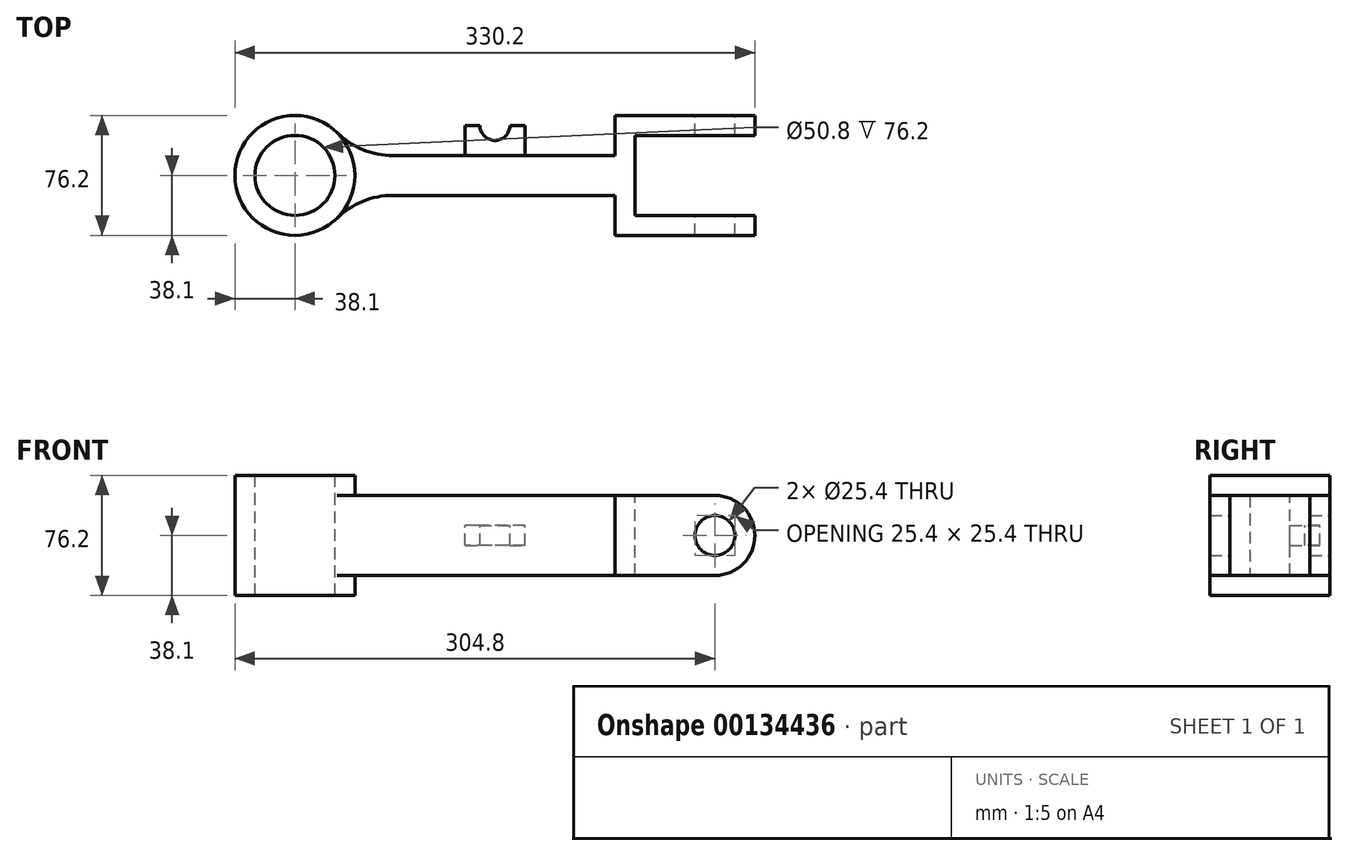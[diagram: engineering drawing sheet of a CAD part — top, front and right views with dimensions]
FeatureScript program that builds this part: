
annotation { "Feature Type Name" : "Feature", "Feature Type Description" : "" }
export const myFeature = defineFeature(function(context is Context, id is Id, definition is map)
    precondition{}
    {
        {
            var Q0;
            Q0=qCreatedBy(makeId("Top.planeOp"),FACE);
            var sketch = newSketch(context, id + "F0", { "sketchPlane" : qUnion([Q0])});
            skCircle(sketch, "E0", {"center": v(0, 0) * mm, "radius": 38.1 * mm});
            skLineSegment(sketch, "E1", {"start": v(35.92, -12.7) * mm, "end": v(203.2, -12.7) * mm});
            skLineSegment(sketch, "E2", {"start": v(35.92, 12.7) * mm, "end": v(203.2, 12.7) * mm});
            skLineSegment(sketch, "E3", {"start": v(203.2, -12.7) * mm, "end": v(203.2, -38.1) * mm});
            skLineSegment(sketch, "E4", {"start": v(203.2, -38.1) * mm, "end": v(279.4, -38.1) * mm});
            skLineSegment(sketch, "E5", {"start": v(279.4, -38.1) * mm, "end": v(279.4, -25.4) * mm});
            skLineSegment(sketch, "E6", {"start": v(279.4, -25.4) * mm, "end": v(215.9, -25.4) * mm});
            skLineSegment(sketch, "E7", {"start": v(215.9, -25.4) * mm, "end": v(215.9, 25.4) * mm});
            skLineSegment(sketch, "E8", {"start": v(215.9, 25.4) * mm, "end": v(279.4, 25.4) * mm});
            skLineSegment(sketch, "E9", {"start": v(279.4, 25.4) * mm, "end": v(279.4, 38.1) * mm});
            skLineSegment(sketch, "E10", {"start": v(279.4, 38.1) * mm, "end": v(203.2, 38.1) * mm});
            skLineSegment(sketch, "E11", {"start": v(203.2, 38.1) * mm, "end": v(203.2, 12.7) * mm});
            skCircle(sketch, "E12", {"center": v(0, 0) * mm, "radius": 25.4 * mm});
            skSolve(sketch);
        }
        {
            var Q0;
            Q0=makeQuery(id+"F0.imprint","IMPRINT",FACE,{"disambiguationData":[TD([[makeQuery(id+"F0.imprint","IMPRINT",EDGE,{"derivedFrom":sQuery(id+"F0.wireOp",EDGE,"E12")}),-1.0]])]});
            var Q1;
            {var subQ0=sQuery(id+"F0.wireOp",EDGE,"E1");Q1=makeQuery(id+"F0.imprint","IMPRINT",FACE,{"disambiguationData":[TD([[makeQuery(id+"F0.imprint","IMPRINT",EDGE,{"derivedFrom":subQ0}),1.0]])]});}
            extrude(context, id + "F1", {"entities" : qUnion([Q0, Q1]), "oppositeDirection" : true, "depth" : 76.2 * mm});
        }
        {
            var Q0;
            Q0=makeQuery(id+"F1.opExtrude","CAP_FACE",FACE,{"disambiguationData":[OSD([sQuery(id+"F0.wireOp",EDGE,"E0"),sQuery(id+"F0.wireOp",EDGE,"E1"),sQuery(id+"F0.wireOp",EDGE,"E2"),sQuery(id+"F0.wireOp",EDGE,"E3"),sQuery(id+"F0.wireOp",EDGE,"E4"),sQuery(id+"F0.wireOp",EDGE,"E5"),sQuery(id+"F0.wireOp",EDGE,"E6"),sQuery(id+"F0.wireOp",EDGE,"E7"),sQuery(id+"F0.wireOp",EDGE,"E8"),sQuery(id+"F0.wireOp",EDGE,"E9"),sQuery(id+"F0.wireOp",EDGE,"E10"),sQuery(id+"F0.wireOp",EDGE,"E11"),sQuery(id+"F0.wireOp",EDGE,"E12")])],"isStart":true});
            var sketch = newSketch(context, id + "F2", { "sketchPlane" : qUnion([Q0])});
            skLineSegment(sketch, "E13", {"start": v(279.4, 25.4) * mm, "end": v(279.4, 38.1) * mm});
            skLineSegment(sketch, "E14", {"start": v(279.4, 38.1) * mm, "end": v(203.2, 38.1) * mm});
            skLineSegment(sketch, "E15", {"start": v(203.2, 38.1) * mm, "end": v(203.2, 12.7) * mm});
            skLineSegment(sketch, "E16", {"start": v(203.2, 12.7) * mm, "end": v(35.92, 12.7) * mm});
            skLineSegment(sketch, "E17", {"start": v(279.4, 25.4) * mm, "end": v(215.9, 25.4) * mm});
            skLineSegment(sketch, "E18", {"start": v(215.9, 25.4) * mm, "end": v(215.9, -25.4) * mm});
            skLineSegment(sketch, "E19", {"start": v(215.9, -25.4) * mm, "end": v(279.4, -25.4) * mm});
            skLineSegment(sketch, "E20", {"start": v(279.4, -25.4) * mm, "end": v(279.4, -38.1) * mm});
            skLineSegment(sketch, "E21", {"start": v(279.4, -38.1) * mm, "end": v(203.2, -38.1) * mm});
            skLineSegment(sketch, "E22", {"start": v(203.2, -38.1) * mm, "end": v(203.2, -12.7) * mm});
            skLineSegment(sketch, "E23", {"start": v(203.2, -12.7) * mm, "end": v(35.92, -12.7) * mm});
            skLineSegment(sketch, "E24", {"start": v(35.92, 12.7) * mm, "end": v(35.92, -12.7) * mm});
            skSolve(sketch);
        }
        {
            var Q0;
            Q0 = qSketchRegion(id + "F2", true);
            extrude(context, id + "F3", {"entities" : qUnion([Q0]), "operationType" : NewBodyOperationType.REMOVE, "oppositeDirection" : true, "depth" : 12.7 * mm});
        }
        {
            var Q0;
            Q0=makeQuery(id+"F1.opExtrude","CAP_FACE",FACE,{"disambiguationData":[OSD([sQuery(id+"F0.wireOp",EDGE,"E0"),sQuery(id+"F0.wireOp",EDGE,"E1"),sQuery(id+"F0.wireOp",EDGE,"E2"),sQuery(id+"F0.wireOp",EDGE,"E3"),sQuery(id+"F0.wireOp",EDGE,"E4"),sQuery(id+"F0.wireOp",EDGE,"E5"),sQuery(id+"F0.wireOp",EDGE,"E6"),sQuery(id+"F0.wireOp",EDGE,"E7"),sQuery(id+"F0.wireOp",EDGE,"E8"),sQuery(id+"F0.wireOp",EDGE,"E9"),sQuery(id+"F0.wireOp",EDGE,"E10"),sQuery(id+"F0.wireOp",EDGE,"E11"),sQuery(id+"F0.wireOp",EDGE,"E12")])],"isStart":false});
            var sketch = newSketch(context, id + "F4", { "sketchPlane" : qUnion([Q0])});
            skLineSegment(sketch, "E25", {"start": v(279.4, 38.1) * mm, "end": v(203.2, 38.1) * mm});
            skLineSegment(sketch, "E26", {"start": v(203.2, 38.1) * mm, "end": v(203.2, 12.7) * mm});
            skLineSegment(sketch, "E27", {"start": v(203.2, 12.7) * mm, "end": v(35.92, 12.7) * mm});
            skLineSegment(sketch, "E28", {"start": v(35.92, 12.7) * mm, "end": v(35.92, -12.7) * mm});
            skLineSegment(sketch, "E29", {"start": v(35.92, -12.7) * mm, "end": v(203.2, -12.7) * mm});
            skLineSegment(sketch, "E30", {"start": v(203.2, -12.7) * mm, "end": v(203.2, -38.1) * mm});
            skLineSegment(sketch, "E31", {"start": v(203.2, -38.1) * mm, "end": v(279.4, -38.1) * mm});
            skLineSegment(sketch, "E32", {"start": v(279.4, -38.1) * mm, "end": v(279.4, -25.4) * mm});
            skLineSegment(sketch, "E33", {"start": v(279.4, -25.4) * mm, "end": v(215.9, -25.4) * mm});
            skLineSegment(sketch, "E34", {"start": v(215.9, -25.4) * mm, "end": v(215.9, 25.4) * mm});
            skLineSegment(sketch, "E35", {"start": v(215.9, 25.4) * mm, "end": v(279.4, 25.4) * mm});
            skLineSegment(sketch, "E36", {"start": v(279.4, 25.4) * mm, "end": v(279.4, 38.1) * mm});
            skSolve(sketch);
        }
        {
            var Q0;
            Q0 = qSketchRegion(id + "F4", true);
            extrude(context, id + "F5", {"entities" : qUnion([Q0]), "operationType" : NewBodyOperationType.REMOVE, "oppositeDirection" : true, "depth" : 12.7 * mm});
        }
        {
            var Q0;
            Q0=makeQuery(id+"F5.boolean.opBoolean","SPLIT",EDGE,{"derivedFrom":makeQuery(id+"F3.boolean.opBoolean","SPLIT",EDGE,{"derivedFrom":makeQuery(id+"F1.opExtrude","SWEPT_EDGE",EDGE,{"disambiguationData":[OSD([sQuery(id+"F0.wireOp",EDGE,"E0"),sQuery(id+"F0.wireOp",EDGE,"E1")])]})})});
            var Q1;
            Q1=makeQuery(id+"F5.boolean.opBoolean","SPLIT",EDGE,{"derivedFrom":makeQuery(id+"F3.boolean.opBoolean","SPLIT",EDGE,{"derivedFrom":makeQuery(id+"F1.opExtrude","SWEPT_EDGE",EDGE,{"disambiguationData":[OSD([sQuery(id+"F0.wireOp",EDGE,"E0"),sQuery(id+"F0.wireOp",EDGE,"E2")])]})})});
            fillet(context, id + "F6", {"entities" : qUnion([Q0, Q1]), "radius" : 50.8 * mm, "tangentPropagation" : true, "allowEdgeOverflow" : false});
        }
        {
            var Q0;
            Q0=makeQuery(id+"F1.opExtrude","CAP_FACE",FACE,{"disambiguationData":[OSD([sQuery(id+"F0.wireOp",EDGE,"E0"),sQuery(id+"F0.wireOp",EDGE,"E1"),sQuery(id+"F0.wireOp",EDGE,"E2"),sQuery(id+"F0.wireOp",EDGE,"E3"),sQuery(id+"F0.wireOp",EDGE,"E4"),sQuery(id+"F0.wireOp",EDGE,"E5"),sQuery(id+"F0.wireOp",EDGE,"E6"),sQuery(id+"F0.wireOp",EDGE,"E7"),sQuery(id+"F0.wireOp",EDGE,"E8"),sQuery(id+"F0.wireOp",EDGE,"E9"),sQuery(id+"F0.wireOp",EDGE,"E10"),sQuery(id+"F0.wireOp",EDGE,"E11"),sQuery(id+"F0.wireOp",EDGE,"E12")])],"isStart":true});
            var sketch = newSketch(context, id + "F7", { "sketchPlane" : qUnion([Q0])});
            skCircle(sketch, "E37", {"center": v(0, 0) * mm, "radius": 38.1 * mm});
            skLineSegment(sketch, "E38", {"start": v(35.92, -12.7) * mm, "end": v(35.92, 12.7) * mm});
            skSolve(sketch);
        }
        {
            var Q0;
            {var subQ0=sQuery(id+"F7.wireOp",EDGE,"E38");Q0=makeQuery(id+"F7.imprint","IMPRINT",FACE,{"disambiguationData":[TD([[makeQuery(id+"F7.imprint","IMPRINT",EDGE,{"derivedFrom":subQ0}),1.0]])]});}
            extrude(context, id + "F8", {"entities" : qUnion([Q0]), "operationType" : NewBodyOperationType.ADD, "oppositeDirection" : true, "depth" : 76.2 * mm});
        }
        {
            var Q0;
            Q0=makeQuery(id+"F1.opExtrude","SWEPT_FACE",FACE,{"disambiguationData":[OSD([sQuery(id+"F0.wireOp",EDGE,"E4")])]});
            var sketch = newSketch(context, id + "F9", { "sketchPlane" : qUnion([Q0])});
            skLineSegment(sketch, "E39", {"start": v(266.7, -12.7) * mm, "end": v(203.2, -12.7) * mm});
            skLineSegment(sketch, "E40", {"start": v(203.2, -12.7) * mm, "end": v(203.2, -63.5) * mm});
            skLineSegment(sketch, "E41", {"start": v(203.2, -63.5) * mm, "end": v(266.7, -63.5) * mm});
            skArc(sketch, "E42", {"start": v(266.7, -12.7) * mm, "mid": v(292.1, -38.1) * mm, "end": v(266.7, -63.5) * mm});
            skSolve(sketch);
        }
        {
            var Q0;
            Q0 = qSketchRegion(id + "F9", true);
            extrude(context, id + "F10", {"entities" : qUnion([Q0]), "operationType" : NewBodyOperationType.ADD, "oppositeDirection" : true, "depth" : 12.7 * mm});
        }
        {
            var Q0;
            Q0=makeQuery(id+"F10.boolean.opBoolean","MERGE",FACE,{"derivedFrom":[makeQuery(id+"F1.opExtrude","SWEPT_FACE",FACE,{"disambiguationData":[OSD([sQuery(id+"F0.wireOp",EDGE,"E4")])]}),makeQuery(id+"F10.opExtrude","CAP_FACE",FACE,{"disambiguationData":[OSD([sQuery(id+"F9.wireOp",EDGE,"E39"),sQuery(id+"F9.wireOp",EDGE,"E40"),sQuery(id+"F9.wireOp",EDGE,"E41"),sQuery(id+"F9.wireOp",EDGE,"E42")])],"isStart":true})]});
            var sketch = newSketch(context, id + "F11", { "sketchPlane" : qUnion([Q0])});
            skLineSegment(sketch, "E43", {"start": v(279.4, -60.1) * mm, "end": v(279.4, -63.5) * mm});
            skLineSegment(sketch, "E44", {"start": v(279.4, -63.5) * mm, "end": v(266.71, -63.5) * mm});
            skArc(sketch, "E45.0", {"start": v(266.7, -12.7) * mm, "mid": v(292.1, -38.1) * mm, "end": v(266.7, -63.5) * mm});
            skLineSegment(sketch, "E46", {"start": v(266.7, -12.7) * mm, "end": v(279.4, -12.7) * mm});
            skLineSegment(sketch, "E47", {"start": v(279.4, -12.7) * mm, "end": v(279.4, -16.1) * mm});
            skSolve(sketch);
        }
        {
            var Q0;
            Q0 = qSketchRegion(id + "F11", true);
            var Q1;
            {var subQ0=sQuery(id+"F9.wireOp",EDGE,"E42");var subQ1=makeQuery(id+"F3.boolean.opBoolean","COPY",EDGE,{"derivedFrom":makeQuery(id+"F3.opExtrude","CAP_EDGE",EDGE,{"disambiguationData":[OSD([sQuery(id+"F2.wireOp",EDGE,"E21")])],"isStart":false})});var subQ2=makeQuery(id+"F9.imprint","INTERSECT",VERTEX,{"derivedFrom":[subQ1,sQuery(id+"F9.wireOp",EDGE,"E39"),subQ0]});Q1=makeQuery(id+"F9.imprint","IMPRINT",FACE,{"disambiguationData":[TD([[makeQuery(id+"F9.imprint","IMPRINT",EDGE,{"disambiguationData":[TD([[subQ2,-1.0]])],"derivedFrom":subQ0}),1.0]])]});}
            var Q2;
            {var subQ0=sQuery(id+"F9.wireOp",EDGE,"E42");var subQ1=makeQuery(id+"F5.boolean.opBoolean","COPY",EDGE,{"derivedFrom":makeQuery(id+"F5.opExtrude","CAP_EDGE",EDGE,{"disambiguationData":[OSD([sQuery(id+"F4.wireOp",EDGE,"E25")])],"isStart":false})});var subQ2=makeQuery(id+"F9.imprint","INTERSECT",VERTEX,{"derivedFrom":[subQ1,sQuery(id+"F9.wireOp",EDGE,"E41"),subQ0]});Q2=makeQuery(id+"F9.imprint","IMPRINT",FACE,{"disambiguationData":[TD([[makeQuery(id+"F9.imprint","IMPRINT",EDGE,{"disambiguationData":[TD([[subQ2,1.0]])],"derivedFrom":subQ0}),1.0]])]});}
            extrude(context, id + "F12", {"entities" : qUnion([Q0, Q1, Q2]), "operationType" : NewBodyOperationType.REMOVE, "oppositeDirection" : true, "depth" : 84.6 * mm});
        }
        {
            var Q0;
            Q0=makeQuery(id+"F1.opExtrude","SWEPT_FACE",FACE,{"disambiguationData":[OSD([sQuery(id+"F0.wireOp",EDGE,"E10")])]});
            var sketch = newSketch(context, id + "F13", { "sketchPlane" : qUnion([Q0])});
            skArc(sketch, "E48.0", {"start": v(-266.7, -12.7) * mm, "mid": v(-292.1, -38.1) * mm, "end": v(-266.7, -63.5) * mm});
            skLineSegment(sketch, "E49", {"start": v(-279.4, -16.1) * mm, "end": v(-279.4, -60.1) * mm});
            skSolve(sketch);
        }
        {
            var Q0;
            Q0 = qSketchRegion(id + "F13", true);
            extrude(context, id + "F14", {"entities" : qUnion([Q0]), "operationType" : NewBodyOperationType.ADD, "oppositeDirection" : true, "depth" : 12.7 * mm});
        }
        {
            var Q0;
            Q0=makeQuery(id+"F14.boolean.opBoolean","MERGE",FACE,{"derivedFrom":[makeQuery(id+"F1.opExtrude","SWEPT_FACE",FACE,{"disambiguationData":[OSD([sQuery(id+"F0.wireOp",EDGE,"E10")])]}),makeQuery(id+"F14.opExtrude","CAP_FACE",FACE,{"disambiguationData":[OSD([sQuery(id+"F13.wireOp",EDGE,"E48.0"),sQuery(id+"F13.wireOp",EDGE,"E49")])],"isStart":true})]});
            var sketch = newSketch(context, id + "F15", { "sketchPlane" : qUnion([Q0])});
            skCircle(sketch, "E50", {"center": v(-266.7, -38.1) * mm, "radius": 12.7 * mm});
            skSolve(sketch);
        }
        {
            var Q0;
            Q0 = qSketchRegion(id + "F15", true);
            extrude(context, id + "F16", {"entities" : qUnion([Q0]), "operationType" : NewBodyOperationType.REMOVE, "endBound" : BoundingType.THROUGH_ALL, "oppositeDirection" : true, "depth" : 25.4 * mm});
        }
        {
            var Q0;
            Q0=makeQuery(id+"F3.boolean.opBoolean","COPY",FACE,{"derivedFrom":makeQuery(id+"F3.opExtrude","CAP_FACE",FACE,{"disambiguationData":[OSD([sQuery(id+"F2.wireOp",EDGE,"E13"),sQuery(id+"F2.wireOp",EDGE,"E14"),sQuery(id+"F2.wireOp",EDGE,"E15"),sQuery(id+"F2.wireOp",EDGE,"E16"),sQuery(id+"F2.wireOp",EDGE,"E17"),sQuery(id+"F2.wireOp",EDGE,"E18"),sQuery(id+"F2.wireOp",EDGE,"E19"),sQuery(id+"F2.wireOp",EDGE,"E20"),sQuery(id+"F2.wireOp",EDGE,"E21"),sQuery(id+"F2.wireOp",EDGE,"E22"),sQuery(id+"F2.wireOp",EDGE,"E23"),sQuery(id+"F2.wireOp",EDGE,"E24")])],"isStart":false})});
            var sketch = newSketch(context, id + "F17", { "sketchPlane" : qUnion([Q0])});
            skLineSegment(sketch, "E51", {"start": v(107.95, 12.7) * mm, "end": v(107.95, 31.75) * mm});
            skLineSegment(sketch, "E52", {"start": v(107.95, 31.75) * mm, "end": v(146.05, 31.75) * mm});
            skLineSegment(sketch, "E53", {"start": v(146.05, 31.75) * mm, "end": v(146.05, 12.7) * mm});
            skLineSegment(sketch, "E54", {"start": v(146.05, 12.7) * mm, "end": v(107.95, 12.7) * mm});
            skArc(sketch, "E55", {"start": v(107.95, 31.75) * mm, "mid": v(127, 50.8) * mm, "end": v(146.05, 31.75) * mm});
            skCircle(sketch, "E56", {"center": v(127, 31.75) * mm, "radius": 9.53 * mm});
            skSolve(sketch);
        }
        {
            var Q0;
            {var subQ5=sQuery(id+"F17.wireOp",EDGE,"E51");Q0=makeQuery(id+"F17.imprint","IMPRINT",FACE,{"disambiguationData":[TD([[makeQuery(id+"F17.imprint","IMPRINT",EDGE,{"derivedFrom":subQ5}),-1.0]])]});}
            var Q1;
            {var subQ0=sQuery(id+"F17.wireOp",EDGE,"E55");Q1=makeQuery(id+"F17.imprint","IMPRINT",FACE,{"disambiguationData":[TD([[makeQuery(id+"F17.imprint","IMPRINT",EDGE,{"derivedFrom":subQ0}),-1.0]])]});}
            extrude(context, id + "F18", {"entities" : qUnion([Q0, Q1]), "operationType" : NewBodyOperationType.ADD, "oppositeDirection" : true, "depth" : 50.8 * mm});
        }
        {
            var Q0;
            Q0=makeQuery(id+"F18.boolean.opBoolean","MERGE",FACE,{"derivedFrom":[makeQuery(id+"F5.boolean.opBoolean","COPY",FACE,{"derivedFrom":makeQuery(id+"F5.opExtrude","CAP_FACE",FACE,{"disambiguationData":[OSD([sQuery(id+"F4.wireOp",EDGE,"E25"),sQuery(id+"F4.wireOp",EDGE,"E26"),sQuery(id+"F4.wireOp",EDGE,"E27"),sQuery(id+"F4.wireOp",EDGE,"E28"),sQuery(id+"F4.wireOp",EDGE,"E29"),sQuery(id+"F4.wireOp",EDGE,"E30"),sQuery(id+"F4.wireOp",EDGE,"E31"),sQuery(id+"F4.wireOp",EDGE,"E32"),sQuery(id+"F4.wireOp",EDGE,"E33"),sQuery(id+"F4.wireOp",EDGE,"E34"),sQuery(id+"F4.wireOp",EDGE,"E35"),sQuery(id+"F4.wireOp",EDGE,"E36")])],"isStart":false})}),makeQuery(id+"F18.opExtrude","CAP_FACE",FACE,{"disambiguationData":[OSD([sQuery(id+"F17.wireOp",EDGE,"E51"),sQuery(id+"F17.wireOp",EDGE,"E53"),sQuery(id+"F17.wireOp",EDGE,"E54"),sQuery(id+"F17.wireOp",EDGE,"E55"),sQuery(id+"F17.wireOp",EDGE,"E56")])],"isStart":false})]});
            var sketch = newSketch(context, id + "F19", { "sketchPlane" : qUnion([Q0])});
            skLineSegment(sketch, "E57.0", {"start": v(146.05, -31.75) * mm, "end": v(146.05, -12.7) * mm});
            skArc(sketch, "E57.1", {"start": v(107.95, -31.75) * mm, "mid": v(127, -50.8) * mm, "end": v(146.05, -31.75) * mm});
            skLineSegment(sketch, "E57.2", {"start": v(107.95, -12.7) * mm, "end": v(107.95, -31.75) * mm});
            skCircle(sketch, "E57.3", {"center": v(127, -31.75) * mm, "radius": 9.53 * mm});
            skLineSegment(sketch, "E58", {"start": v(146.05, -12.7) * mm, "end": v(107.95, -12.7) * mm});
            skSolve(sketch);
        }
        {
            var Q0;
            Q0 = qSketchRegion(id + "F19", true);
            extrude(context, id + "F20", {"entities" : qUnion([Q0]), "operationType" : NewBodyOperationType.REMOVE, "oppositeDirection" : true, "depth" : 19.05 * mm});
        }
        {
            var Q0;
            Q0=makeQuery(id+"F18.boolean.opBoolean","MERGE",FACE,{"derivedFrom":[makeQuery(id+"F3.boolean.opBoolean","COPY",FACE,{"derivedFrom":makeQuery(id+"F3.opExtrude","CAP_FACE",FACE,{"disambiguationData":[OSD([sQuery(id+"F2.wireOp",EDGE,"E13"),sQuery(id+"F2.wireOp",EDGE,"E14"),sQuery(id+"F2.wireOp",EDGE,"E15"),sQuery(id+"F2.wireOp",EDGE,"E16"),sQuery(id+"F2.wireOp",EDGE,"E17"),sQuery(id+"F2.wireOp",EDGE,"E18"),sQuery(id+"F2.wireOp",EDGE,"E19"),sQuery(id+"F2.wireOp",EDGE,"E20"),sQuery(id+"F2.wireOp",EDGE,"E21"),sQuery(id+"F2.wireOp",EDGE,"E22"),sQuery(id+"F2.wireOp",EDGE,"E23"),sQuery(id+"F2.wireOp",EDGE,"E24")])],"isStart":false})}),makeQuery(id+"F18.opExtrude","CAP_FACE",FACE,{"disambiguationData":[OSD([sQuery(id+"F17.wireOp",EDGE,"E51"),sQuery(id+"F17.wireOp",EDGE,"E53"),sQuery(id+"F17.wireOp",EDGE,"E54"),sQuery(id+"F17.wireOp",EDGE,"E55"),sQuery(id+"F17.wireOp",EDGE,"E56")])],"isStart":true})]});
            var sketch = newSketch(context, id + "F21", { "sketchPlane" : qUnion([Q0])});
            skArc(sketch, "E59.0", {"start": v(107.95, 31.75) * mm, "mid": v(127, 50.8) * mm, "end": v(146.05, 31.75) * mm});
            skLineSegment(sketch, "E59.1", {"start": v(107.95, 12.7) * mm, "end": v(107.95, 31.75) * mm});
            skCircle(sketch, "E59.2", {"center": v(127, 31.75) * mm, "radius": 9.53 * mm});
            skLineSegment(sketch, "E59.3", {"start": v(146.05, 31.75) * mm, "end": v(146.05, 12.7) * mm});
            skLineSegment(sketch, "E59.4", {"start": v(146.05, 12.7) * mm, "end": v(107.95, 12.7) * mm});
            skSolve(sketch);
        }
        {
            var Q0;
            Q0 = qSketchRegion(id + "F21", true);
            extrude(context, id + "F22", {"entities" : qUnion([Q0]), "operationType" : NewBodyOperationType.REMOVE, "oppositeDirection" : true, "depth" : 19.05 * mm});
        }
    });
